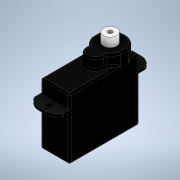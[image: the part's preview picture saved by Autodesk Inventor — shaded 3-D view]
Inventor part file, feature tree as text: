
AUTODESK INVENTOR PART (.ipt)
format: ipt  version: 2022 (Build 260153000, 153)  size: 909,824 bytes
history: native  units: in
note: dims shown in document units (in); Inventor stores cm internally (conversion verified against a paired STEP export)
features: extrude x7, projected_geometry x6, sketch x5, fillet x4
ambient origin geometry x8: Origin, YZ Plane, XZ Plane, XY Plane, X Axis, Y Axis, Z Axis, Center Point
bodies: Solid1 (feature_tree)
feature tree (22):
  extrude  "Extrusion1"  Depth=0.7874in
  extrude  "Extrusion2"  Depth=0.3346in
  extrude  "Extrusion3"  Depth=0.1181in TaperAngle=0.0deg
  sketch  "Sketch4"  dims[d9=0.1496in d10=0.0512in]
  extrude  "Extrusion4"  Depth=0.0512in
  extrude  "Extrusion5"  Depth=0.0197in TaperAngle=0.0deg
  fillet  "Fillet1"  Radius=0.1457in
  fillet  "Fillet2"  Radius=0.126in
  fillet  "Fillet3"  Radius=0.126in
  sketch  "Sketch5"  dims[d12=53.1496in d14=360.0deg d16=0.1024in d17=0.0in d18=0.1457in d19=0.126in d20=0.126in d21=0.1831in d22=0.0in d23=0.1516in d24=0.0in d25=0.0197in d26=0.0197in d27=0.0197in d28=0.1516in d29=0.0in d30=0.3937in d31=0.0in d32=0.0197in]
  extrude  "Extrusion6"  Depth=0.0197in TaperAngle=0.0deg
  extrude  "Extrusion7"  Depth=0.0197in TaperAngle=0.0deg
  fillet  "Fillet4"  Radius=0.0197in
  sketch  "Sketch1"  dims[d0=0.3248in d1=0.7874in]
  sketch  "Sketch2"  dims[d2=0.689in d3=0.0in d5=0.3346in]
  projected_geometry  "Projected Loop1"
  sketch  "Sketch3"  dims[d6=0.1969in d7=0.1181in d8=0.0in]
  projected_geometry  "Projected Loop2"
  projected_geometry  "Projected Loop3"
  projected_geometry  "Projected Loop4"
  projected_geometry  "Projected Loop5"
  projected_geometry  "Projected Loop6"
